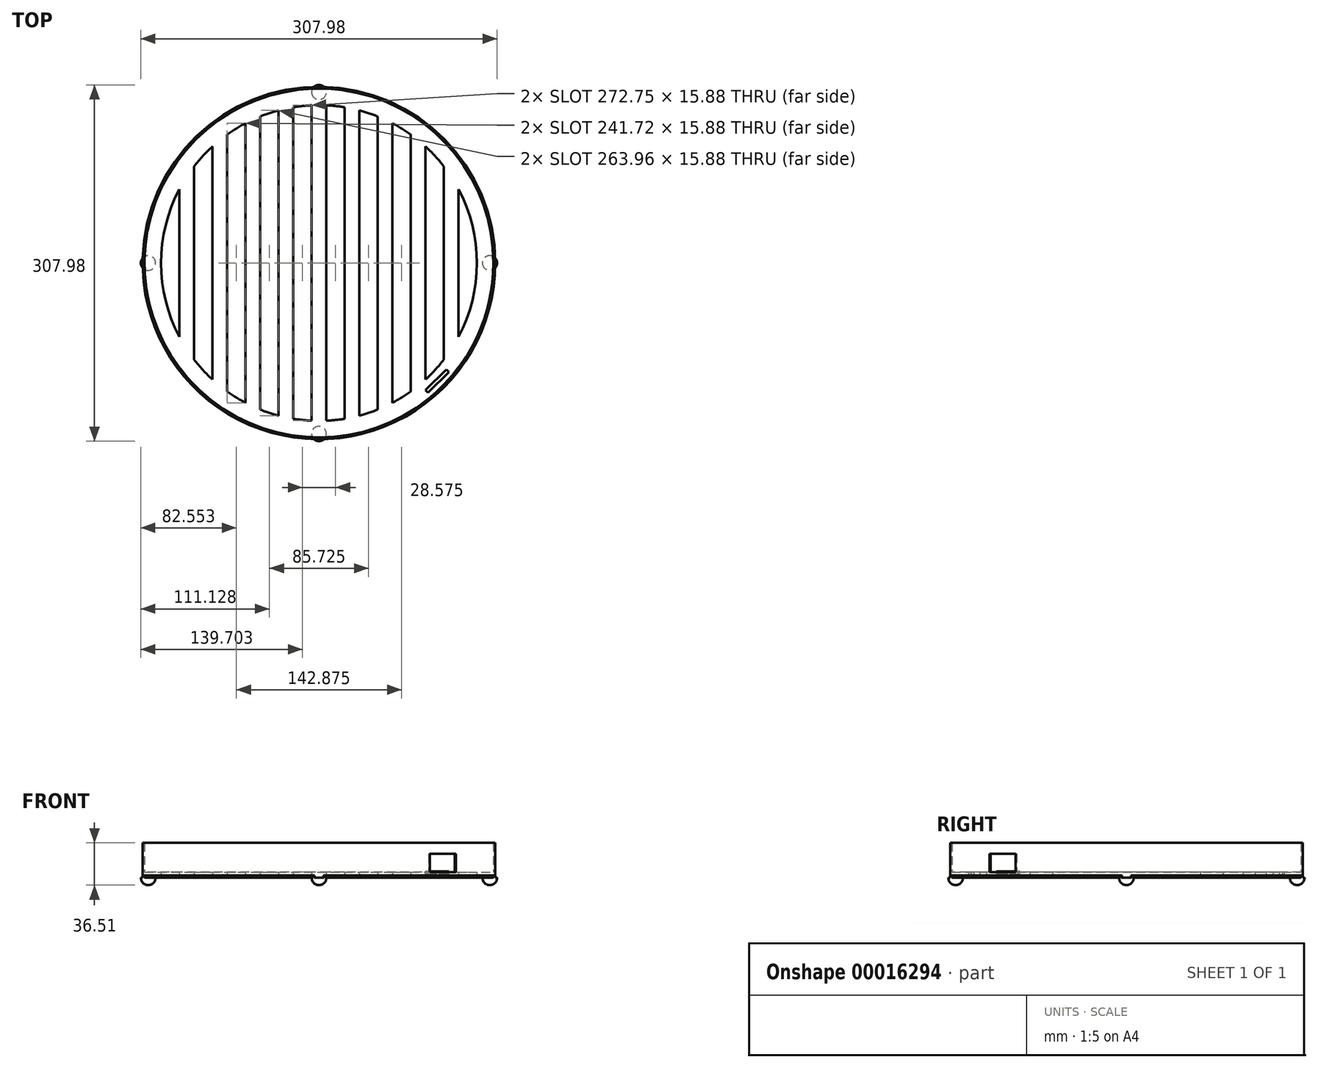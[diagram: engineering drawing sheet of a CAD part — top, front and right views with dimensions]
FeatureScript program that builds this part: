
annotation { "Feature Type Name" : "Feature", "Feature Type Description" : "" }
export const myFeature = defineFeature(function(context is Context, id is Id, definition is map)
    precondition{}
    {
        {
            var Q0;
            Q0=qCreatedBy(makeId("Top.planeOp"),FACE);
            var sketch = newSketch(context, id + "F0", { "sketchPlane" : qUnion([Q0])});
            skCircle(sketch, "E0", {"center": v(0, 0) * mm, "radius": 152.4 * mm});
            skArc(sketch, "E1", {"start": v(-120.65, 63.9) * mm, "mid": v(-136.53, 0) * mm, "end": v(-120.65, -63.9) * mm});
            skLineSegment(sketch, "E2.0", {"start": v(-6.35, 136.53) * mm, "end": v(-6.35, 136.38) * mm});
            skLineSegment(sketch, "E3.0", {"start": v(6.35, 136.53) * mm, "end": v(6.35, 136.38) * mm});
            skLineSegment(sketch, "E4.trimOffspring", {"start": v(6.35, 136.38) * mm, "end": v(6.35, -136.38) * mm});
            skLineSegment(sketch, "E5.trimOffspring", {"start": v(-6.35, 136.38) * mm, "end": v(-6.35, -136.38) * mm});
            skLineSegment(sketch, "E6.trimOffspring", {"start": v(-6.35, -136.38) * mm, "end": v(-6.35, -136.53) * mm});
            skLineSegment(sketch, "E7.trimOffspring", {"start": v(6.35, -136.38) * mm, "end": v(6.35, -136.53) * mm});
            skLineSegment(sketch, "E8.1.0.0", {"start": v(34.92, 131.98) * mm, "end": v(34.92, -131.98) * mm});
            skLineSegment(sketch, "E8.1.0.1", {"start": v(22.23, 134.7) * mm, "end": v(22.23, -134.7) * mm});
            skLineSegment(sketch, "E8.2.0.0", {"start": v(63.5, 120.86) * mm, "end": v(63.5, -120.86) * mm});
            skLineSegment(sketch, "E8.2.0.1", {"start": v(50.8, 126.72) * mm, "end": v(50.8, -126.72) * mm});
            skLineSegment(sketch, "E8.3.0.0", {"start": v(92.07, 100.8) * mm, "end": v(92.07, -100.8) * mm});
            skLineSegment(sketch, "E8.3.0.1", {"start": v(79.38, 111.08) * mm, "end": v(79.38, -111.08) * mm});
            skLineSegment(sketch, "E8.4.0.0", {"start": v(120.65, 63.9) * mm, "end": v(120.65, -63.9) * mm});
            skLineSegment(sketch, "E8.4.0.1", {"start": v(107.95, 83.58) * mm, "end": v(107.95, -83.58) * mm});
            skPoint(sketch, "E9.orphan", {"position": v(120.65, 15.12) * mm});
            skPoint(sketch, "E10.orphan", {"position": v(107.95, 15.12) * mm});
            skPoint(sketch, "E11.orphan", {"position": v(92.07, 15.12) * mm});
            skPoint(sketch, "E12.orphan", {"position": v(79.38, -12.17) * mm});
            skPoint(sketch, "E13.orphan", {"position": v(92.07, -12.17) * mm});
            skPoint(sketch, "E14.orphan", {"position": v(107.95, -12.17) * mm});
            skPoint(sketch, "E15.orphan", {"position": v(120.65, -12.17) * mm});
            skPoint(sketch, "E16.orphan", {"position": v(79.38, 15.12) * mm});
            skPoint(sketch, "E17.orphan", {"position": v(63.5, 15.12) * mm});
            skPoint(sketch, "E18.orphan", {"position": v(50.8, 15.12) * mm});
            skPoint(sketch, "E19.orphan", {"position": v(34.92, 15.12) * mm});
            skPoint(sketch, "E20.orphan", {"position": v(22.23, 15.12) * mm});
            skPoint(sketch, "E21.orphan", {"position": v(6.35, 15.12) * mm});
            skPoint(sketch, "E22.orphan", {"position": v(-6.35, 15.12) * mm});
            skPoint(sketch, "E23.orphan", {"position": v(63.5, -12.17) * mm});
            skPoint(sketch, "E24.orphan", {"position": v(50.8, -12.17) * mm});
            skPoint(sketch, "E25.orphan", {"position": v(22.23, -12.17) * mm});
            skPoint(sketch, "E26.orphan", {"position": v(-6.35, -12.17) * mm});
            skLineSegment(sketch, "E27.MirrorCS", {"start": v(-22.23, 134.7) * mm, "end": v(-22.23, -134.7) * mm});
            skLineSegment(sketch, "E28.MirrorCS", {"start": v(-34.92, 131.98) * mm, "end": v(-34.92, -131.98) * mm});
            skLineSegment(sketch, "E29.MirrorCS", {"start": v(-50.8, 126.72) * mm, "end": v(-50.8, -126.72) * mm});
            skLineSegment(sketch, "E30.MirrorCS", {"start": v(-63.5, 120.86) * mm, "end": v(-63.5, -120.86) * mm});
            skLineSegment(sketch, "E31.MirrorCS", {"start": v(-79.38, 111.08) * mm, "end": v(-79.38, -111.08) * mm});
            skLineSegment(sketch, "E32.MirrorCS", {"start": v(-92.07, 100.8) * mm, "end": v(-92.07, -100.8) * mm});
            skLineSegment(sketch, "E33.MirrorCS", {"start": v(-107.95, 83.58) * mm, "end": v(-107.95, -83.58) * mm});
            skLineSegment(sketch, "E34.MirrorCS", {"start": v(-120.65, 63.9) * mm, "end": v(-120.65, -63.9) * mm});
            skArc(sketch, "E35.trimOffspring", {"start": v(-107.95, -83.58) * mm, "mid": v(-100.38, -92.53) * mm, "end": v(-92.07, -100.8) * mm});
            skArc(sketch, "E36.trimOffspring", {"start": v(-79.37, -111.08) * mm, "mid": v(-71.6, -116.24) * mm, "end": v(-63.5, -120.86) * mm});
            skArc(sketch, "E37.trimOffspring", {"start": v(-92.07, 100.8) * mm, "mid": v(-100.38, 92.53) * mm, "end": v(-107.95, 83.58) * mm});
            skArc(sketch, "E38.trimOffspring", {"start": v(-63.5, 120.86) * mm, "mid": v(-71.6, 116.24) * mm, "end": v(-79.37, 111.08) * mm});
            skArc(sketch, "E39.trimOffspring", {"start": v(-50.8, -126.72) * mm, "mid": v(-42.94, -129.6) * mm, "end": v(-34.92, -131.98) * mm});
            skArc(sketch, "E40.trimOffspring", {"start": v(-34.92, 131.98) * mm, "mid": v(-42.94, 129.6) * mm, "end": v(-50.8, 126.72) * mm});
            skArc(sketch, "E41.trimOffspring", {"start": v(-22.23, -134.7) * mm, "mid": v(-14.31, -135.77) * mm, "end": v(-6.35, -136.38) * mm});
            skArc(sketch, "E42.trimOffspring", {"start": v(6.35, -136.38) * mm, "mid": v(14.31, -135.77) * mm, "end": v(22.22, -134.7) * mm});
            skArc(sketch, "E43.trimOffspring", {"start": v(34.92, -131.98) * mm, "mid": v(42.94, -129.6) * mm, "end": v(50.8, -126.72) * mm});
            skArc(sketch, "E44.trimOffspring", {"start": v(63.5, -120.86) * mm, "mid": v(71.6, -116.24) * mm, "end": v(79.38, -111.08) * mm});
            skArc(sketch, "E45.trimOffspring", {"start": v(92.07, -100.8) * mm, "mid": v(100.38, -92.53) * mm, "end": v(107.95, -83.58) * mm});
            skArc(sketch, "E46.trimOffspring", {"start": v(120.65, -63.9) * mm, "mid": v(136.52, 0) * mm, "end": v(120.65, 63.9) * mm});
            skArc(sketch, "E47.trimOffspring", {"start": v(107.95, 83.58) * mm, "mid": v(100.38, 92.53) * mm, "end": v(92.07, 100.8) * mm});
            skArc(sketch, "E48.trimOffspring", {"start": v(79.37, 111.08) * mm, "mid": v(71.6, 116.24) * mm, "end": v(63.5, 120.86) * mm});
            skArc(sketch, "E49.trimOffspring", {"start": v(50.8, 126.72) * mm, "mid": v(42.94, 129.6) * mm, "end": v(34.92, 131.98) * mm});
            skArc(sketch, "E50.trimOffspring", {"start": v(22.22, 134.7) * mm, "mid": v(14.31, 135.77) * mm, "end": v(6.35, 136.38) * mm});
            skArc(sketch, "E51.trimOffspring", {"start": v(-6.35, 136.38) * mm, "mid": v(-14.31, 135.77) * mm, "end": v(-22.23, 134.7) * mm});
            skPoint(sketch, "E52.start.orphan", {"position": v(0, 136.53) * mm});
            skPoint(sketch, "E53.orphan", {"position": v(6.35, -12.17) * mm});
            skSolve(sketch);
        }
        {
            var Q0;
            Q0 = qSketchRegion(id + "F0", true);
            extrude(context, id + "F1", {"entities" : qUnion([Q0]), "depth" : 4.76 * mm});
        }
        {
            var Q0;
            Q0=makeQuery(id+"F1.opExtrude","CAP_FACE",FACE,{"disambiguationData":[OSD([sQuery(id+"F0.wireOp",EDGE,"E0"),sQuery(id+"F0.wireOp",EDGE,"E1"),sQuery(id+"F0.wireOp",EDGE,"E4.trimOffspring"),sQuery(id+"F0.wireOp",EDGE,"E5.trimOffspring"),sQuery(id+"F0.wireOp",EDGE,"E8.1.0.0"),sQuery(id+"F0.wireOp",EDGE,"E8.1.0.1"),sQuery(id+"F0.wireOp",EDGE,"E8.2.0.0"),sQuery(id+"F0.wireOp",EDGE,"E8.2.0.1"),sQuery(id+"F0.wireOp",EDGE,"E8.3.0.0"),sQuery(id+"F0.wireOp",EDGE,"E8.3.0.1"),sQuery(id+"F0.wireOp",EDGE,"E8.4.0.0"),sQuery(id+"F0.wireOp",EDGE,"E8.4.0.1"),sQuery(id+"F0.wireOp",EDGE,"E27.MirrorCS"),sQuery(id+"F0.wireOp",EDGE,"E28.MirrorCS"),sQuery(id+"F0.wireOp",EDGE,"E29.MirrorCS"),sQuery(id+"F0.wireOp",EDGE,"E30.MirrorCS"),sQuery(id+"F0.wireOp",EDGE,"E31.MirrorCS"),sQuery(id+"F0.wireOp",EDGE,"E32.MirrorCS"),sQuery(id+"F0.wireOp",EDGE,"E33.MirrorCS"),sQuery(id+"F0.wireOp",EDGE,"E34.MirrorCS"),sQuery(id+"F0.wireOp",EDGE,"E35.trimOffspring"),sQuery(id+"F0.wireOp",EDGE,"E36.trimOffspring"),sQuery(id+"F0.wireOp",EDGE,"E37.trimOffspring"),sQuery(id+"F0.wireOp",EDGE,"E38.trimOffspring"),sQuery(id+"F0.wireOp",EDGE,"E39.trimOffspring"),sQuery(id+"F0.wireOp",EDGE,"E40.trimOffspring"),sQuery(id+"F0.wireOp",EDGE,"E41.trimOffspring"),sQuery(id+"F0.wireOp",EDGE,"E42.trimOffspring"),sQuery(id+"F0.wireOp",EDGE,"E43.trimOffspring"),sQuery(id+"F0.wireOp",EDGE,"E44.trimOffspring"),sQuery(id+"F0.wireOp",EDGE,"E45.trimOffspring"),sQuery(id+"F0.wireOp",EDGE,"E46.trimOffspring"),sQuery(id+"F0.wireOp",EDGE,"E47.trimOffspring"),sQuery(id+"F0.wireOp",EDGE,"E48.trimOffspring"),sQuery(id+"F0.wireOp",EDGE,"E49.trimOffspring"),sQuery(id+"F0.wireOp",EDGE,"E50.trimOffspring"),sQuery(id+"F0.wireOp",EDGE,"E51.trimOffspring")])],"isStart":true});
            var sketch = newSketch(context, id + "F2", { "sketchPlane" : qUnion([Q0])});
            skCircle(sketch, "E54", {"center": v(0, 147.64) * mm, "radius": 6.35 * mm});
            skPoint(sketch, "E55.start.orphan", {"position": v(0, 153.99) * mm});
            skCircle(sketch, "E56.1.0", {"center": v(-147.64, 0) * mm, "radius": 6.35 * mm});
            skCircle(sketch, "E56.2.0", {"center": v(0, -147.64) * mm, "radius": 6.35 * mm});
            skCircle(sketch, "E56.3.0", {"center": v(147.64, 0) * mm, "radius": 6.35 * mm});
            skPoint(sketch, "E56.center", {"position": v(0, 0) * mm});
            skSolve(sketch);
        }
        {
            var Q0;
            Q0 = qSketchRegion(id + "F2", true);
            extrude(context, id + "F3", {"entities" : qUnion([Q0]), "operationType" : NewBodyOperationType.ADD, "depth" : 6.35 * mm});
        }
        {
            var Q0;
            Q0=makeQuery(id+"F3.opExtrude","CAP_EDGE",EDGE,{"disambiguationData":[OSD([sQuery(id+"F2.wireOp",EDGE,"E54")])],"isStart":false});
            var Q1;
            Q1=makeQuery(id+"F3.opExtrude","CAP_EDGE",EDGE,{"disambiguationData":[OSD([sQuery(id+"F2.wireOp",EDGE,"E56.3.0")])],"isStart":false});
            var Q2;
            Q2=makeQuery(id+"F3.opExtrude","CAP_EDGE",EDGE,{"disambiguationData":[OSD([sQuery(id+"F2.wireOp",EDGE,"E56.2.0")])],"isStart":false});
            var Q3;
            Q3=makeQuery(id+"F3.opExtrude","CAP_EDGE",EDGE,{"disambiguationData":[OSD([sQuery(id+"F2.wireOp",EDGE,"E56.1.0")])],"isStart":false});
            fillet(context, id + "F4", {"entities" : qUnion([Q0, Q1, Q2, Q3]), "radius" : 6.35 * mm, "tangentPropagation" : true, "allowEdgeOverflow" : false});
        }
        {
            var Q0;
            {var subQ0=sQuery(id+"F0.wireOp",EDGE,"E0");var subQ1=sQuery(id+"F2.wireOp",EDGE,"E54");Q0=makeQuery(id+"F3.boolean.opBoolean","SPLIT",EDGE,{"disambiguationData":[TD([makeQuery(id+"F1.opExtrude","SWEPT_FACE",FACE,{"disambiguationData":[OSD([subQ0])]}),makeQuery(id+"F1.opExtrude","CAP_FACE",FACE,{"disambiguationData":[OSD([subQ0,sQuery(id+"F0.wireOp",EDGE,"E1"),sQuery(id+"F0.wireOp",EDGE,"E4.trimOffspring"),sQuery(id+"F0.wireOp",EDGE,"E5.trimOffspring"),sQuery(id+"F0.wireOp",EDGE,"E8.1.0.0"),sQuery(id+"F0.wireOp",EDGE,"E8.1.0.1"),sQuery(id+"F0.wireOp",EDGE,"E8.2.0.0"),sQuery(id+"F0.wireOp",EDGE,"E8.2.0.1"),sQuery(id+"F0.wireOp",EDGE,"E8.3.0.0"),sQuery(id+"F0.wireOp",EDGE,"E8.3.0.1"),sQuery(id+"F0.wireOp",EDGE,"E8.4.0.0"),sQuery(id+"F0.wireOp",EDGE,"E8.4.0.1"),sQuery(id+"F0.wireOp",EDGE,"E27.MirrorCS"),sQuery(id+"F0.wireOp",EDGE,"E28.MirrorCS"),sQuery(id+"F0.wireOp",EDGE,"E29.MirrorCS"),sQuery(id+"F0.wireOp",EDGE,"E30.MirrorCS"),sQuery(id+"F0.wireOp",EDGE,"E31.MirrorCS"),sQuery(id+"F0.wireOp",EDGE,"E32.MirrorCS"),sQuery(id+"F0.wireOp",EDGE,"E33.MirrorCS"),sQuery(id+"F0.wireOp",EDGE,"E34.MirrorCS"),sQuery(id+"F0.wireOp",EDGE,"E35.trimOffspring"),sQuery(id+"F0.wireOp",EDGE,"E36.trimOffspring"),sQuery(id+"F0.wireOp",EDGE,"E37.trimOffspring"),sQuery(id+"F0.wireOp",EDGE,"E38.trimOffspring"),sQuery(id+"F0.wireOp",EDGE,"E39.trimOffspring"),sQuery(id+"F0.wireOp",EDGE,"E40.trimOffspring"),sQuery(id+"F0.wireOp",EDGE,"E41.trimOffspring"),sQuery(id+"F0.wireOp",EDGE,"E42.trimOffspring"),sQuery(id+"F0.wireOp",EDGE,"E43.trimOffspring"),sQuery(id+"F0.wireOp",EDGE,"E44.trimOffspring"),sQuery(id+"F0.wireOp",EDGE,"E45.trimOffspring"),sQuery(id+"F0.wireOp",EDGE,"E46.trimOffspring"),sQuery(id+"F0.wireOp",EDGE,"E47.trimOffspring"),sQuery(id+"F0.wireOp",EDGE,"E48.trimOffspring"),sQuery(id+"F0.wireOp",EDGE,"E49.trimOffspring"),sQuery(id+"F0.wireOp",EDGE,"E50.trimOffspring"),sQuery(id+"F0.wireOp",EDGE,"E51.trimOffspring")])],"isStart":true}),makeQuery(id+"F3.opExtrude","SWEPT_FACE",FACE,{"disambiguationData":[OSD([subQ1])]}),makeQuery(id+"F3.opExtrude","CAP_FACE",FACE,{"disambiguationData":[OSD([subQ1])],"isStart":true})])],"derivedFrom":makeQuery(id+"F1.opExtrude","CAP_EDGE",EDGE,{"disambiguationData":[OSD([subQ0])],"isStart":true})});}
            var Q1;
            {var subQ0=sQuery(id+"F0.wireOp",EDGE,"E0");var subQ1=sQuery(id+"F2.wireOp",EDGE,"E56.1.0");Q1=makeQuery(id+"F3.boolean.opBoolean","SPLIT",EDGE,{"disambiguationData":[TD([makeQuery(id+"F1.opExtrude","SWEPT_FACE",FACE,{"disambiguationData":[OSD([subQ0])]}),makeQuery(id+"F1.opExtrude","CAP_FACE",FACE,{"disambiguationData":[OSD([subQ0,sQuery(id+"F0.wireOp",EDGE,"E1"),sQuery(id+"F0.wireOp",EDGE,"E4.trimOffspring"),sQuery(id+"F0.wireOp",EDGE,"E5.trimOffspring"),sQuery(id+"F0.wireOp",EDGE,"E8.1.0.0"),sQuery(id+"F0.wireOp",EDGE,"E8.1.0.1"),sQuery(id+"F0.wireOp",EDGE,"E8.2.0.0"),sQuery(id+"F0.wireOp",EDGE,"E8.2.0.1"),sQuery(id+"F0.wireOp",EDGE,"E8.3.0.0"),sQuery(id+"F0.wireOp",EDGE,"E8.3.0.1"),sQuery(id+"F0.wireOp",EDGE,"E8.4.0.0"),sQuery(id+"F0.wireOp",EDGE,"E8.4.0.1"),sQuery(id+"F0.wireOp",EDGE,"E27.MirrorCS"),sQuery(id+"F0.wireOp",EDGE,"E28.MirrorCS"),sQuery(id+"F0.wireOp",EDGE,"E29.MirrorCS"),sQuery(id+"F0.wireOp",EDGE,"E30.MirrorCS"),sQuery(id+"F0.wireOp",EDGE,"E31.MirrorCS"),sQuery(id+"F0.wireOp",EDGE,"E32.MirrorCS"),sQuery(id+"F0.wireOp",EDGE,"E33.MirrorCS"),sQuery(id+"F0.wireOp",EDGE,"E34.MirrorCS"),sQuery(id+"F0.wireOp",EDGE,"E35.trimOffspring"),sQuery(id+"F0.wireOp",EDGE,"E36.trimOffspring"),sQuery(id+"F0.wireOp",EDGE,"E37.trimOffspring"),sQuery(id+"F0.wireOp",EDGE,"E38.trimOffspring"),sQuery(id+"F0.wireOp",EDGE,"E39.trimOffspring"),sQuery(id+"F0.wireOp",EDGE,"E40.trimOffspring"),sQuery(id+"F0.wireOp",EDGE,"E41.trimOffspring"),sQuery(id+"F0.wireOp",EDGE,"E42.trimOffspring"),sQuery(id+"F0.wireOp",EDGE,"E43.trimOffspring"),sQuery(id+"F0.wireOp",EDGE,"E44.trimOffspring"),sQuery(id+"F0.wireOp",EDGE,"E45.trimOffspring"),sQuery(id+"F0.wireOp",EDGE,"E46.trimOffspring"),sQuery(id+"F0.wireOp",EDGE,"E47.trimOffspring"),sQuery(id+"F0.wireOp",EDGE,"E48.trimOffspring"),sQuery(id+"F0.wireOp",EDGE,"E49.trimOffspring"),sQuery(id+"F0.wireOp",EDGE,"E50.trimOffspring"),sQuery(id+"F0.wireOp",EDGE,"E51.trimOffspring")])],"isStart":true}),makeQuery(id+"F3.opExtrude","SWEPT_FACE",FACE,{"disambiguationData":[OSD([subQ1])]}),makeQuery(id+"F3.opExtrude","CAP_FACE",FACE,{"disambiguationData":[OSD([subQ1])],"isStart":true})])],"derivedFrom":makeQuery(id+"F1.opExtrude","CAP_EDGE",EDGE,{"disambiguationData":[OSD([subQ0])],"isStart":true})});}
            var Q2;
            {var subQ0=sQuery(id+"F0.wireOp",EDGE,"E0");var subQ1=sQuery(id+"F2.wireOp",EDGE,"E56.3.0");Q2=makeQuery(id+"F3.boolean.opBoolean","SPLIT",EDGE,{"disambiguationData":[TD([makeQuery(id+"F1.opExtrude","SWEPT_FACE",FACE,{"disambiguationData":[OSD([subQ0])]}),makeQuery(id+"F1.opExtrude","CAP_FACE",FACE,{"disambiguationData":[OSD([subQ0,sQuery(id+"F0.wireOp",EDGE,"E1"),sQuery(id+"F0.wireOp",EDGE,"E4.trimOffspring"),sQuery(id+"F0.wireOp",EDGE,"E5.trimOffspring"),sQuery(id+"F0.wireOp",EDGE,"E8.1.0.0"),sQuery(id+"F0.wireOp",EDGE,"E8.1.0.1"),sQuery(id+"F0.wireOp",EDGE,"E8.2.0.0"),sQuery(id+"F0.wireOp",EDGE,"E8.2.0.1"),sQuery(id+"F0.wireOp",EDGE,"E8.3.0.0"),sQuery(id+"F0.wireOp",EDGE,"E8.3.0.1"),sQuery(id+"F0.wireOp",EDGE,"E8.4.0.0"),sQuery(id+"F0.wireOp",EDGE,"E8.4.0.1"),sQuery(id+"F0.wireOp",EDGE,"E27.MirrorCS"),sQuery(id+"F0.wireOp",EDGE,"E28.MirrorCS"),sQuery(id+"F0.wireOp",EDGE,"E29.MirrorCS"),sQuery(id+"F0.wireOp",EDGE,"E30.MirrorCS"),sQuery(id+"F0.wireOp",EDGE,"E31.MirrorCS"),sQuery(id+"F0.wireOp",EDGE,"E32.MirrorCS"),sQuery(id+"F0.wireOp",EDGE,"E33.MirrorCS"),sQuery(id+"F0.wireOp",EDGE,"E34.MirrorCS"),sQuery(id+"F0.wireOp",EDGE,"E35.trimOffspring"),sQuery(id+"F0.wireOp",EDGE,"E36.trimOffspring"),sQuery(id+"F0.wireOp",EDGE,"E37.trimOffspring"),sQuery(id+"F0.wireOp",EDGE,"E38.trimOffspring"),sQuery(id+"F0.wireOp",EDGE,"E39.trimOffspring"),sQuery(id+"F0.wireOp",EDGE,"E40.trimOffspring"),sQuery(id+"F0.wireOp",EDGE,"E41.trimOffspring"),sQuery(id+"F0.wireOp",EDGE,"E42.trimOffspring"),sQuery(id+"F0.wireOp",EDGE,"E43.trimOffspring"),sQuery(id+"F0.wireOp",EDGE,"E44.trimOffspring"),sQuery(id+"F0.wireOp",EDGE,"E45.trimOffspring"),sQuery(id+"F0.wireOp",EDGE,"E46.trimOffspring"),sQuery(id+"F0.wireOp",EDGE,"E47.trimOffspring"),sQuery(id+"F0.wireOp",EDGE,"E48.trimOffspring"),sQuery(id+"F0.wireOp",EDGE,"E49.trimOffspring"),sQuery(id+"F0.wireOp",EDGE,"E50.trimOffspring"),sQuery(id+"F0.wireOp",EDGE,"E51.trimOffspring")])],"isStart":true}),makeQuery(id+"F3.opExtrude","SWEPT_FACE",FACE,{"disambiguationData":[OSD([subQ1])]}),makeQuery(id+"F3.opExtrude","CAP_FACE",FACE,{"disambiguationData":[OSD([subQ1])],"isStart":true})])],"derivedFrom":makeQuery(id+"F1.opExtrude","CAP_EDGE",EDGE,{"disambiguationData":[OSD([subQ0])],"isStart":true})});}
            var Q3;
            {var subQ0=sQuery(id+"F0.wireOp",EDGE,"E0");var subQ1=sQuery(id+"F2.wireOp",EDGE,"E56.2.0");Q3=makeQuery(id+"F3.boolean.opBoolean","SPLIT",EDGE,{"disambiguationData":[TD([makeQuery(id+"F1.opExtrude","SWEPT_FACE",FACE,{"disambiguationData":[OSD([subQ0])]}),makeQuery(id+"F1.opExtrude","CAP_FACE",FACE,{"disambiguationData":[OSD([subQ0,sQuery(id+"F0.wireOp",EDGE,"E1"),sQuery(id+"F0.wireOp",EDGE,"E4.trimOffspring"),sQuery(id+"F0.wireOp",EDGE,"E5.trimOffspring"),sQuery(id+"F0.wireOp",EDGE,"E8.1.0.0"),sQuery(id+"F0.wireOp",EDGE,"E8.1.0.1"),sQuery(id+"F0.wireOp",EDGE,"E8.2.0.0"),sQuery(id+"F0.wireOp",EDGE,"E8.2.0.1"),sQuery(id+"F0.wireOp",EDGE,"E8.3.0.0"),sQuery(id+"F0.wireOp",EDGE,"E8.3.0.1"),sQuery(id+"F0.wireOp",EDGE,"E8.4.0.0"),sQuery(id+"F0.wireOp",EDGE,"E8.4.0.1"),sQuery(id+"F0.wireOp",EDGE,"E27.MirrorCS"),sQuery(id+"F0.wireOp",EDGE,"E28.MirrorCS"),sQuery(id+"F0.wireOp",EDGE,"E29.MirrorCS"),sQuery(id+"F0.wireOp",EDGE,"E30.MirrorCS"),sQuery(id+"F0.wireOp",EDGE,"E31.MirrorCS"),sQuery(id+"F0.wireOp",EDGE,"E32.MirrorCS"),sQuery(id+"F0.wireOp",EDGE,"E33.MirrorCS"),sQuery(id+"F0.wireOp",EDGE,"E34.MirrorCS"),sQuery(id+"F0.wireOp",EDGE,"E35.trimOffspring"),sQuery(id+"F0.wireOp",EDGE,"E36.trimOffspring"),sQuery(id+"F0.wireOp",EDGE,"E37.trimOffspring"),sQuery(id+"F0.wireOp",EDGE,"E38.trimOffspring"),sQuery(id+"F0.wireOp",EDGE,"E39.trimOffspring"),sQuery(id+"F0.wireOp",EDGE,"E40.trimOffspring"),sQuery(id+"F0.wireOp",EDGE,"E41.trimOffspring"),sQuery(id+"F0.wireOp",EDGE,"E42.trimOffspring"),sQuery(id+"F0.wireOp",EDGE,"E43.trimOffspring"),sQuery(id+"F0.wireOp",EDGE,"E44.trimOffspring"),sQuery(id+"F0.wireOp",EDGE,"E45.trimOffspring"),sQuery(id+"F0.wireOp",EDGE,"E46.trimOffspring"),sQuery(id+"F0.wireOp",EDGE,"E47.trimOffspring"),sQuery(id+"F0.wireOp",EDGE,"E48.trimOffspring"),sQuery(id+"F0.wireOp",EDGE,"E49.trimOffspring"),sQuery(id+"F0.wireOp",EDGE,"E50.trimOffspring"),sQuery(id+"F0.wireOp",EDGE,"E51.trimOffspring")])],"isStart":true}),makeQuery(id+"F3.opExtrude","SWEPT_FACE",FACE,{"disambiguationData":[OSD([subQ1])]}),makeQuery(id+"F3.opExtrude","CAP_FACE",FACE,{"disambiguationData":[OSD([subQ1])],"isStart":true})])],"derivedFrom":makeQuery(id+"F1.opExtrude","CAP_EDGE",EDGE,{"disambiguationData":[OSD([subQ0])],"isStart":true})});}
            chamfer(context, id + "F5", {"entities" : qUnion([Q0, Q1, Q2, Q3]), "width" : 1.9 * mm, "tangentPropagation" : true});
        }
        {
            var Q0;
            Q0=makeQuery(id+"F1.opExtrude","CAP_FACE",FACE,{"disambiguationData":[OSD([sQuery(id+"F0.wireOp",EDGE,"E0"),sQuery(id+"F0.wireOp",EDGE,"E1"),sQuery(id+"F0.wireOp",EDGE,"E4.trimOffspring"),sQuery(id+"F0.wireOp",EDGE,"E5.trimOffspring"),sQuery(id+"F0.wireOp",EDGE,"E8.1.0.0"),sQuery(id+"F0.wireOp",EDGE,"E8.1.0.1"),sQuery(id+"F0.wireOp",EDGE,"E8.2.0.0"),sQuery(id+"F0.wireOp",EDGE,"E8.2.0.1"),sQuery(id+"F0.wireOp",EDGE,"E8.3.0.0"),sQuery(id+"F0.wireOp",EDGE,"E8.3.0.1"),sQuery(id+"F0.wireOp",EDGE,"E8.4.0.0"),sQuery(id+"F0.wireOp",EDGE,"E8.4.0.1"),sQuery(id+"F0.wireOp",EDGE,"E27.MirrorCS"),sQuery(id+"F0.wireOp",EDGE,"E28.MirrorCS"),sQuery(id+"F0.wireOp",EDGE,"E29.MirrorCS"),sQuery(id+"F0.wireOp",EDGE,"E30.MirrorCS"),sQuery(id+"F0.wireOp",EDGE,"E31.MirrorCS"),sQuery(id+"F0.wireOp",EDGE,"E32.MirrorCS"),sQuery(id+"F0.wireOp",EDGE,"E33.MirrorCS"),sQuery(id+"F0.wireOp",EDGE,"E34.MirrorCS"),sQuery(id+"F0.wireOp",EDGE,"E35.trimOffspring"),sQuery(id+"F0.wireOp",EDGE,"E36.trimOffspring"),sQuery(id+"F0.wireOp",EDGE,"E37.trimOffspring"),sQuery(id+"F0.wireOp",EDGE,"E38.trimOffspring"),sQuery(id+"F0.wireOp",EDGE,"E39.trimOffspring"),sQuery(id+"F0.wireOp",EDGE,"E40.trimOffspring"),sQuery(id+"F0.wireOp",EDGE,"E41.trimOffspring"),sQuery(id+"F0.wireOp",EDGE,"E42.trimOffspring"),sQuery(id+"F0.wireOp",EDGE,"E43.trimOffspring"),sQuery(id+"F0.wireOp",EDGE,"E44.trimOffspring"),sQuery(id+"F0.wireOp",EDGE,"E45.trimOffspring"),sQuery(id+"F0.wireOp",EDGE,"E46.trimOffspring"),sQuery(id+"F0.wireOp",EDGE,"E47.trimOffspring"),sQuery(id+"F0.wireOp",EDGE,"E48.trimOffspring"),sQuery(id+"F0.wireOp",EDGE,"E49.trimOffspring"),sQuery(id+"F0.wireOp",EDGE,"E50.trimOffspring"),sQuery(id+"F0.wireOp",EDGE,"E51.trimOffspring")])],"isStart":false});
            var sketch = newSketch(context, id + "F6", { "sketchPlane" : qUnion([Q0])});
            skSolve(sketch);
        }
        {
            var Q0;
            Q0=makeQuery(id+"F6.imprint","IMPRINT",FACE,{"disambiguationData":[TD([[makeQuery(id+"F6.imprint","IMPRINT",EDGE,{"derivedFrom":makeQuery(id+"F1.opExtrude","CAP_EDGE",EDGE,{"disambiguationData":[OSD([sQuery(id+"F0.wireOp",EDGE,"E0")])],"isStart":false})}),1.0]])]});
            var sketch = newSketch(context, id + "F7", { "sketchPlane" : qUnion([Q0])});
            skLineSegment(sketch, "E57", {"start": v(92.05, -110) * mm, "end": v(110, -92.05) * mm});
            skLineSegment(sketch, "E58.0", {"start": v(94.3, -112.25) * mm, "end": v(112.25, -94.3) * mm});
            skLineSegment(sketch, "E59", {"start": v(110, -92.05) * mm, "end": v(112.25, -94.3) * mm});
            skLineSegment(sketch, "E60", {"start": v(94.3, -112.25) * mm, "end": v(92.05, -110) * mm});
            skSolve(sketch);
        }
        {
            var Q0;
            Q0 = qSketchRegion(id + "F7", true);
            extrude(context, id + "F8", {"entities" : qUnion([Q0]), "operationType" : NewBodyOperationType.REMOVE, "oppositeDirection" : true, "depth" : 25.4 * mm});
        }
        {
            var Q0;
            Q0=makeQuery(id+"F6.imprint","IMPRINT",FACE,{"disambiguationData":[TD([[makeQuery(id+"F6.imprint","IMPRINT",EDGE,{"derivedFrom":makeQuery(id+"F1.opExtrude","CAP_EDGE",EDGE,{"disambiguationData":[OSD([sQuery(id+"F0.wireOp",EDGE,"E0")])],"isStart":false})}),1.0]])]});
            var sketch = newSketch(context, id + "F9", { "sketchPlane" : qUnion([Q0])});
            skCircle(sketch, "E61", {"center": v(0, 0) * mm, "radius": 152.4 * mm});
            skCircle(sketch, "E62.0", {"center": v(0, 0) * mm, "radius": 150.81 * mm});
            skSolve(sketch);
        }
        {
            var Q0;
            Q0 = qSketchRegion(id + "F9", true);
            extrude(context, id + "F10", {"entities" : qUnion([Q0]), "operationType" : NewBodyOperationType.ADD, "depth" : 25.4 * mm});
        }
        {
            var Q0;
            Q0 = qSketchRegion(id + "F7", true);
            extrude(context, id + "F11", {"entities" : qUnion([Q0]), "operationType" : NewBodyOperationType.ADD, "endBound" : BoundingType.SYMMETRIC, "depth" : 3.17 * mm});
        }
        {
            var Q0;
            Q0=makeQuery(id+"F11.opExtrude","SWEPT_FACE",FACE,{"disambiguationData":[OSD([sQuery(id+"F7.wireOp",EDGE,"E57")])]});
            var sketch = newSketch(context, id + "F12", { "sketchPlane" : qUnion([Q0])});
            skLineSegment(sketch, "E63.0", {"start": v(-15.88, 4.76) * mm, "end": v(15.88, 4.76) * mm});
            skLineSegment(sketch, "E64.0", {"start": v(-15.87, 20.64) * mm, "end": v(15.88, 20.64) * mm});
            skLineSegment(sketch, "E65.0", {"start": v(15.88, 4.76) * mm, "end": v(15.88, 20.64) * mm});
            skLineSegment(sketch, "E66.0", {"start": v(-15.88, 4.76) * mm, "end": v(-15.87, 20.64) * mm});
            skPoint(sketch, "E67.orphan", {"position": v(-104.7, 20.64) * mm});
            skPoint(sketch, "E68.orphan", {"position": v(104.7, 20.64) * mm});
            skPoint(sketch, "E69.end.orphan", {"position": v(0, 20.64) * mm});
            skPoint(sketch, "E69.start.orphan", {"position": v(0, 4.76) * mm});
            skSolve(sketch);
        }
        {
            var Q0;
            Q0 = qSketchRegion(id + "F12", true);
            extrude(context, id + "F13", {"entities" : qUnion([Q0]), "operationType" : NewBodyOperationType.REMOVE, "oppositeDirection" : true, "depth" : 25.4 * mm});
        }
        {
            var Q0;
            Q0 = qSketchRegion(id + "F7", true);
            extrude(context, id + "F14", {"entities" : qUnion([Q0]), "operationType" : NewBodyOperationType.ADD, "depth" : 0.64 * mm});
        }
    });
